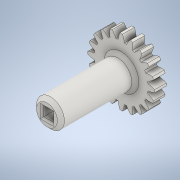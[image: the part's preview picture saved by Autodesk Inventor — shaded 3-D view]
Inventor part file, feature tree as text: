
AUTODESK INVENTOR PART (.ipt)
format: ipt  version: 2022 (Build 260153000, 153)  size: 514,560 bytes
history: native  units: mm (DEFAULTED — no unit token found)
features: sketch x4, extrude x3, plane x3, other x3, chamfer x2
ambient origin geometry x8: Origin, YZ Plane, XZ Plane, XY Plane, X Axis, Y Axis, Z Axis, Center Point
bodies: Solid1 (feature_tree)
feature tree (15):
  extrude  "Extrusion1"  Depth=4.0mm TaperAngle=0.0deg
  plane  "Work Plane1"
  plane  "Work Plane2"
  plane  "Work Plane3"
  other  "Spur Gear"
  extrude  "Extrusion2"  Depth=76.2mm TaperAngle=0.0deg
  extrude  "Extrusion3"  TaperAngle=0.0deg  [1 undecoded]
  chamfer  "Chamfer1"  Distance=25.4mm
  chamfer  "Chamfer2"  Distance=25.4mm
  sketch  "Sketch1"  dims[d0=22.8mm d1=4.0mm d2=0.0mm]
  sketch  "Sketch2"  dims[d3=20.0mm d4=76.2mm d5=0.0mm]
  other  "Srf1"
  sketch  "Sketch3"  dims[d6=0.0mm d7=1.570796mm d9=0.0mm d14=0.0mm d15=25.4mm]
  sketch  "Sketch4"  dims[d16=0.0mm d17=0.0mm d18=0.0mm d19=25.4mm d20=3.375mm d21=0.0mm d22=0.0mm d23=9.525mm d24=25.4mm d25=0.0mm d26=1.2mm d27=3.175mm d28=45.0deg d29=0.6mm d30=3.175mm d31=45.0deg]
  other  "Pitch Diameter"
note: 1 required parameter value undecoded (feature->parameter linkage not recoverable at this tier; creation-order binding heuristic only, values carry confidence <= 0.55)
